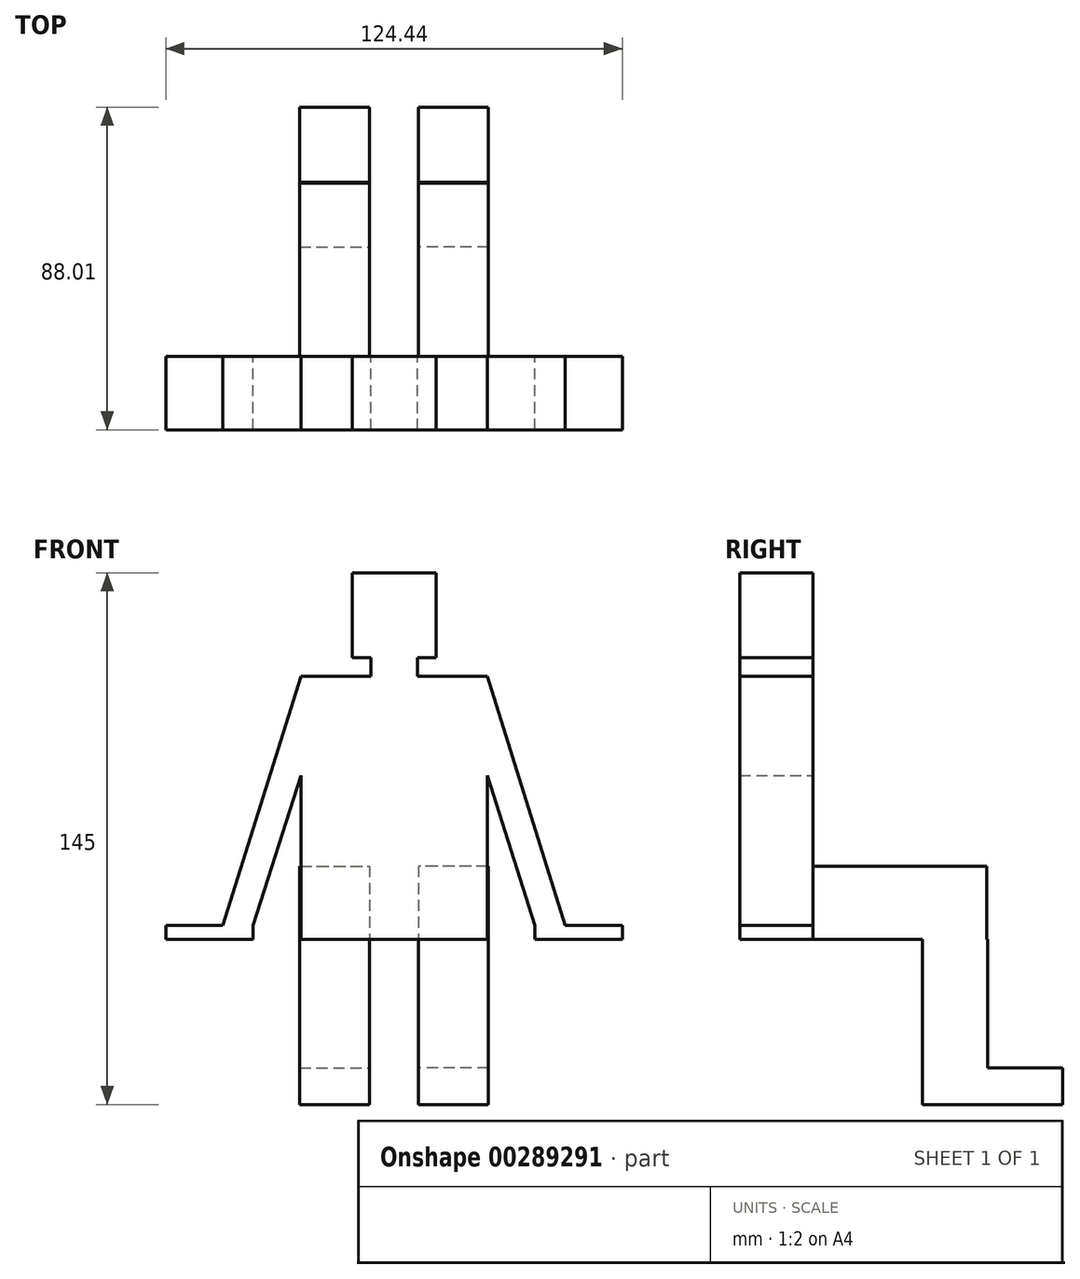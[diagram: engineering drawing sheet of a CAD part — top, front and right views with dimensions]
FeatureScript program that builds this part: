
annotation { "Feature Type Name" : "Feature", "Feature Type Description" : "" }
export const myFeature = defineFeature(function(context is Context, id is Id, definition is map)
    precondition{}
    {
        {
            var Q0;
            Q0=qCreatedBy(makeId("Front.planeOp"),FACE);
            var sketch = newSketch(context, id + "F0", { "sketchPlane" : qUnion([Q0])});
            skLineSegment(sketch, "E0.bottom", {"start": v(-25.4, 71.75) * mm, "end": v(-6.35, 71.75) * mm});
            skLineSegment(sketch, "E0.top", {"start": v(-25.4, 0) * mm, "end": v(0, 0) * mm});
            skLineSegment(sketch, "E0.left", {"start": v(-25.4, 44.76) * mm, "end": v(-25.4, 0) * mm});
            skLineSegment(sketch, "E1.bottom", {"start": v(-62.22, 3.8) * mm, "end": v(-46.67, 3.8) * mm});
            skLineSegment(sketch, "E1.top", {"start": v(-62.22, 0) * mm, "end": v(-38.41, 0) * mm});
            skLineSegment(sketch, "E1.left", {"start": v(-62.22, 3.8) * mm, "end": v(-62.22, 0) * mm});
            skLineSegment(sketch, "E1.right", {"start": v(-38.41, 3.8) * mm, "end": v(-38.41, 0) * mm});
            skLineSegment(sketch, "E2", {"start": v(-25.4, 71.75) * mm, "end": v(-46.67, 3.8) * mm});
            skLineSegment(sketch, "E3", {"start": v(-38.41, 3.8) * mm, "end": v(-25.4, 44.76) * mm});
            skLineSegment(sketch, "E4.left", {"start": v(-6.35, 71.75) * mm, "end": v(-6.35, 76.83) * mm});
            skLineSegment(sketch, "E5", {"start": v(-6.35, 76.83) * mm, "end": v(-11.43, 76.83) * mm});
            skLineSegment(sketch, "E6", {"start": v(-11.43, 76.83) * mm, "end": v(-11.43, 100) * mm});
            skLineSegment(sketch, "E7", {"start": v(-11.43, 100) * mm, "end": v(0, 100) * mm});
            skLineSegment(sketch, "E8.MirrorCS", {"start": v(6.35, 71.75) * mm, "end": v(6.35, 76.83) * mm});
            skLineSegment(sketch, "E9.MirrorCS", {"start": v(6.35, 76.83) * mm, "end": v(11.43, 76.83) * mm});
            skLineSegment(sketch, "E10.MirrorCS", {"start": v(38.41, 3.8) * mm, "end": v(38.41, 0) * mm});
            skLineSegment(sketch, "E11.MirrorCS", {"start": v(62.22, 3.8) * mm, "end": v(62.22, 0) * mm});
            skLineSegment(sketch, "E12.MirrorCS", {"start": v(38.41, 3.8) * mm, "end": v(25.4, 44.76) * mm});
            skLineSegment(sketch, "E13.MirrorCS", {"start": v(25.4, 71.75) * mm, "end": v(46.67, 3.8) * mm});
            skLineSegment(sketch, "E14.MirrorCS", {"start": v(25.4, 71.75) * mm, "end": v(6.35, 71.75) * mm});
            skLineSegment(sketch, "E15.MirrorCS", {"start": v(62.22, 0) * mm, "end": v(38.41, 0) * mm});
            skLineSegment(sketch, "E16.MirrorCS", {"start": v(62.22, 3.8) * mm, "end": v(46.67, 3.8) * mm});
            skLineSegment(sketch, "E17.MirrorCS", {"start": v(11.43, 76.83) * mm, "end": v(11.43, 100) * mm});
            skLineSegment(sketch, "E18.MirrorCS", {"start": v(25.4, 44.76) * mm, "end": v(25.4, 0) * mm});
            skLineSegment(sketch, "E19.MirrorCS", {"start": v(11.43, 100) * mm, "end": v(0, 100) * mm});
            skLineSegment(sketch, "E20.MirrorCS", {"start": v(25.4, 0) * mm, "end": v(0, 0) * mm});
            skSolve(sketch);
        }
        {
            var Q0;
            Q0=makeQuery(id+"F0.imprint","IMPRINT",FACE,{"disambiguationData":[TD([[makeQuery(id+"F0.imprint","IMPRINT",EDGE,{"derivedFrom":sQuery(id+"F0.wireOp",EDGE,"E0.bottom")}),-1.0]])]});
            extrude(context, id + "F1", {"entities" : qUnion([Q0]), "depth" : 20 * mm});
        }
        {
            var Q0;
            Q0=qCreatedBy(makeId("Top.planeOp"),FACE);
            var sketch = newSketch(context, id + "F2", { "sketchPlane" : qUnion([Q0])});
            skLineSegment(sketch, "E21.bottom", {"start": v(-25.71, 0) * mm, "end": v(-6.69, 0) * mm});
            skLineSegment(sketch, "E21.top", {"start": v(-25.71, 47.31) * mm, "end": v(-6.69, 47.31) * mm});
            skLineSegment(sketch, "E21.left", {"start": v(-25.71, 0) * mm, "end": v(-25.71, 47.31) * mm});
            skLineSegment(sketch, "E21.right", {"start": v(-6.69, 0) * mm, "end": v(-6.69, 47.31) * mm});
            skLineSegment(sketch, "E22.MirrorCS", {"start": v(25.71, 0) * mm, "end": v(6.69, 0) * mm});
            skLineSegment(sketch, "E23.MirrorCS", {"start": v(25.71, 47.31) * mm, "end": v(6.69, 47.31) * mm});
            skLineSegment(sketch, "E24.MirrorCS", {"start": v(6.69, 0) * mm, "end": v(6.69, 47.31) * mm});
            skLineSegment(sketch, "E25.MirrorCS", {"start": v(25.71, 0) * mm, "end": v(25.71, 47.31) * mm});
            skSolve(sketch);
        }
        {
            var Q0;
            Q0=makeQuery(id+"F2.imprint","IMPRINT",FACE,{"disambiguationData":[TD([[makeQuery(id+"F2.imprint","IMPRINT",EDGE,{"derivedFrom":sQuery(id+"F2.wireOp",EDGE,"E21.bottom")}),1.0]])]});
            var Q1;
            Q1=makeQuery(id+"F2.imprint","IMPRINT",FACE,{"disambiguationData":[TD([[makeQuery(id+"F2.imprint","IMPRINT",EDGE,{"derivedFrom":sQuery(id+"F2.wireOp",EDGE,"E22.MirrorCS")}),-1.0]])]});
            extrude(context, id + "F3", {"entities" : qUnion([Q0, Q1]), "operationType" : NewBodyOperationType.ADD, "depth" : 20 * mm});
        }
        {
            var Q0;
            Q0=qCreatedBy(makeId("Top.planeOp"),FACE);
            var sketch = newSketch(context, id + "F4", { "sketchPlane" : qUnion([Q0])});
            skLineSegment(sketch, "E26.bottom", {"start": v(25.71, 47.57) * mm, "end": v(6.69, 47.57) * mm});
            skLineSegment(sketch, "E26.top", {"start": v(25.71, 29.83) * mm, "end": v(6.69, 29.83) * mm});
            skLineSegment(sketch, "E26.left", {"start": v(25.71, 47.57) * mm, "end": v(25.71, 29.83) * mm});
            skLineSegment(sketch, "E26.right", {"start": v(6.69, 47.57) * mm, "end": v(6.69, 29.83) * mm});
            skLineSegment(sketch, "E27.MirrorCS", {"start": v(-6.69, 47.57) * mm, "end": v(-6.69, 29.83) * mm});
            skLineSegment(sketch, "E28.MirrorCS", {"start": v(-25.71, 47.57) * mm, "end": v(-25.71, 29.83) * mm});
            skLineSegment(sketch, "E29.MirrorCS", {"start": v(-25.71, 47.57) * mm, "end": v(-6.69, 47.57) * mm});
            skLineSegment(sketch, "E30.MirrorCS", {"start": v(-25.71, 29.83) * mm, "end": v(-6.69, 29.83) * mm});
            skSolve(sketch);
        }
        {
            var Q0;
            Q0=makeQuery(id+"F4.imprint","IMPRINT",FACE,{"disambiguationData":[TD([[makeQuery(id+"F4.imprint","IMPRINT",EDGE,{"derivedFrom":sQuery(id+"F4.wireOp",EDGE,"E26.bottom")}),1.0]])]});
            var Q1;
            Q1=makeQuery(id+"F4.imprint","IMPRINT",FACE,{"disambiguationData":[TD([[makeQuery(id+"F4.imprint","IMPRINT",EDGE,{"derivedFrom":sQuery(id+"F4.wireOp",EDGE,"E27.MirrorCS")}),-1.0]])]});
            extrude(context, id + "F5", {"entities" : qUnion([Q0, Q1]), "operationType" : NewBodyOperationType.ADD, "oppositeDirection" : true, "depth" : 35 * mm});
        }
        {
            var Q0;
            Q0=makeQuery(id+"F5.opExtrude","CAP_FACE",FACE,{"disambiguationData":[OSD([sQuery(id+"F4.wireOp",EDGE,"E26.bottom"),sQuery(id+"F4.wireOp",EDGE,"E26.top"),sQuery(id+"F4.wireOp",EDGE,"E26.left"),sQuery(id+"F4.wireOp",EDGE,"E26.right")])],"isStart":false});
            var sketch = newSketch(context, id + "F6", { "sketchPlane" : qUnion([Q0])});
            skLineSegment(sketch, "E31.bottom", {"start": v(25.71, -29.83) * mm, "end": v(6.69, -29.83) * mm});
            skLineSegment(sketch, "E31.top", {"start": v(25.71, -68.01) * mm, "end": v(6.69, -68.01) * mm});
            skLineSegment(sketch, "E31.left", {"start": v(25.71, -29.83) * mm, "end": v(25.71, -68.01) * mm});
            skLineSegment(sketch, "E31.right", {"start": v(6.69, -29.83) * mm, "end": v(6.69, -68.01) * mm});
            skLineSegment(sketch, "E32.MirrorCS", {"start": v(-25.71, -29.83) * mm, "end": v(-25.71, -68.01) * mm});
            skLineSegment(sketch, "E33.MirrorCS", {"start": v(-6.69, -29.83) * mm, "end": v(-6.69, -68.01) * mm});
            skLineSegment(sketch, "E34.MirrorCS", {"start": v(-25.71, -68.01) * mm, "end": v(-6.69, -68.01) * mm});
            skLineSegment(sketch, "E35.MirrorCS", {"start": v(-25.71, -29.83) * mm, "end": v(-6.69, -29.83) * mm});
            skSolve(sketch);
        }
        {
            var Q0;
            {var subQ0=sQuery(id+"F6.wireOp",EDGE,"E31.top");Q0=makeQuery(id+"F6.imprint","IMPRINT",FACE,{"disambiguationData":[TD([[makeQuery(id+"F6.imprint","IMPRINT",EDGE,{"derivedFrom":subQ0}),-1.0]])]});}
            var Q1;
            Q1=makeQuery(id+"F6.imprint","IMPRINT",FACE,{"disambiguationData":[TD([[makeQuery(id+"F6.imprint","IMPRINT",EDGE,{"derivedFrom":sQuery(id+"F6.wireOp",EDGE,"E32.MirrorCS")}),1.0]])]});
            var Q2;
            {var subQ0=sQuery(id+"F6.wireOp",EDGE,"E31.bottom");Q2=makeQuery(id+"F6.imprint","IMPRINT",FACE,{"disambiguationData":[TD([[makeQuery(id+"F6.imprint","IMPRINT",EDGE,{"derivedFrom":subQ0}),1.0]])]});}
            extrude(context, id + "F7", {"entities" : qUnion([Q0, Q1, Q2]), "operationType" : NewBodyOperationType.ADD, "depth" : 10 * mm});
        }
    });
